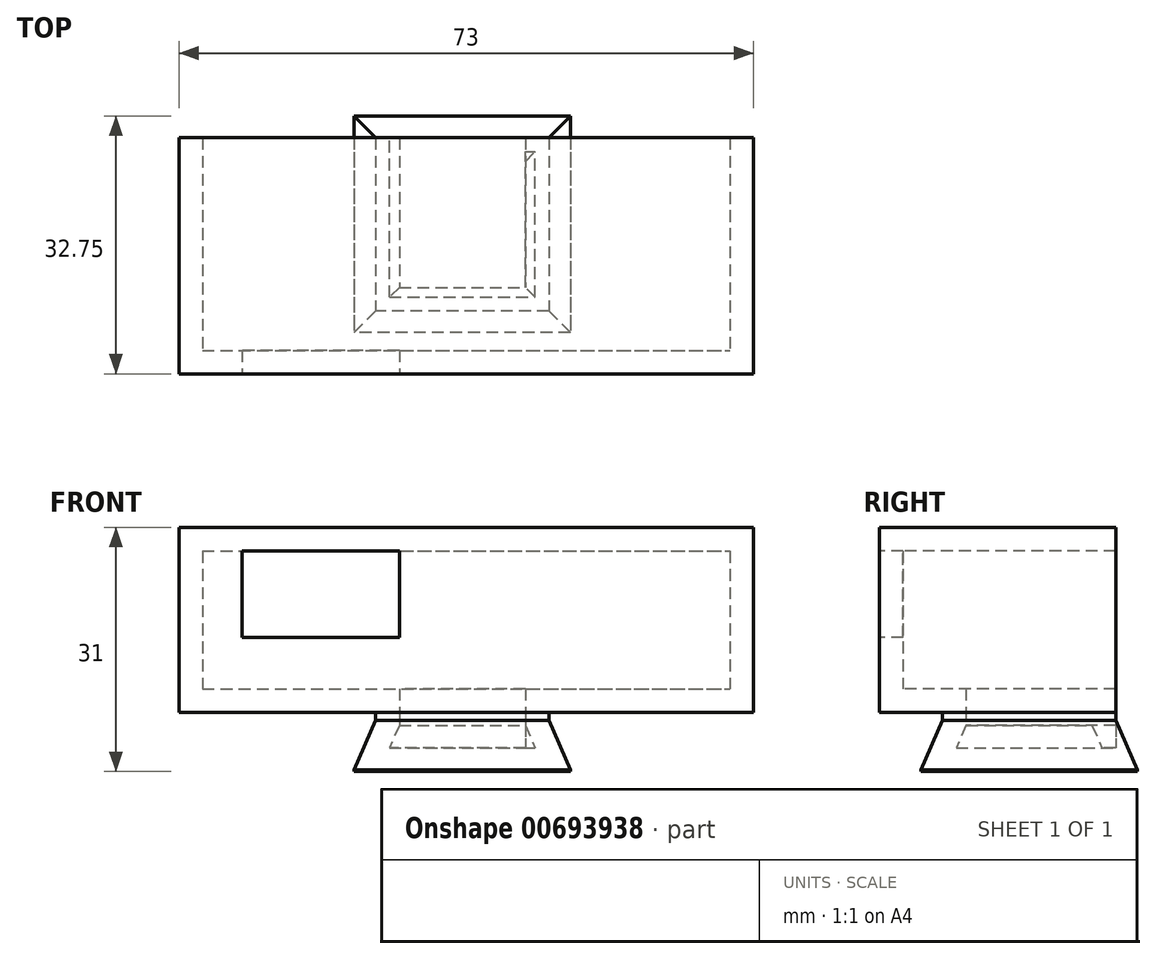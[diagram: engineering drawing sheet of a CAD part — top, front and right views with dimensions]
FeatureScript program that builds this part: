
annotation { "Feature Type Name" : "Feature", "Feature Type Description" : "" }
export const myFeature = defineFeature(function(context is Context, id is Id, definition is map)
    precondition{}
    {
        {
            var Q0;
            Q0=qCreatedBy(makeId("Top.planeOp"),FACE);
            var sketch = newSketch(context, id + "F0", { "sketchPlane" : qUnion([Q0])});
            skLineSegment(sketch, "E0.bottom", {"start": v(13.75, 13.75) * mm, "end": v(-13.75, 13.75) * mm});
            skLineSegment(sketch, "E0.top", {"start": v(13.75, -13.75) * mm, "end": v(-13.75, -13.75) * mm});
            skLineSegment(sketch, "E0.left", {"start": v(13.75, 13.75) * mm, "end": v(13.75, -13.75) * mm});
            skLineSegment(sketch, "E0.right", {"start": v(-13.75, 13.75) * mm, "end": v(-13.75, -13.75) * mm});
            skPoint(sketch, "E0.middle", {"position": v(0, 0) * mm});
            skLineSegment(sketch, "E1.bottom", {"start": v(11, 11) * mm, "end": v(-11, 11) * mm});
            skLineSegment(sketch, "E1.top", {"start": v(11, -11) * mm, "end": v(-11, -11) * mm});
            skLineSegment(sketch, "E1.left", {"start": v(11, 11) * mm, "end": v(11, -11) * mm});
            skLineSegment(sketch, "E1.right", {"start": v(-11, 11) * mm, "end": v(-11, -11) * mm});
            skLineSegment(sketch, "E2.bottom", {"start": v(-36, 11) * mm, "end": v(37, 11) * mm});
            skLineSegment(sketch, "E2.top", {"start": v(-36, -19) * mm, "end": v(37, -19) * mm});
            skLineSegment(sketch, "E2.left", {"start": v(-36, 11) * mm, "end": v(-36, -19) * mm});
            skLineSegment(sketch, "E2.right", {"start": v(37, 11) * mm, "end": v(37, -19) * mm});
            skSolve(sketch);
        }
        {
            var Q0;
            Q0=makeQuery(id+"F0.imprint","IMPRINT",FACE,{"disambiguationData":[TD([[makeQuery(id+"F0.imprint","IMPRINT",EDGE,{"derivedFrom":sQuery(id+"F0.wireOp",EDGE,"E1.bottom")}),1.0]])]});
            extrude(context, id + "F1", {"entities" : qUnion([Q0]), "depth" : 7.5 * mm, "offsetDistance" : 25 * mm, "hasSecondDirection" : true, "secondDirectionOppositeDirection" : false, "secondDirectionDepth" : 6.5 * mm});
        }
        {
            var Q0;
            {var subQ2=sQuery(id+"F0.wireOp",EDGE,"E0.bottom");Q0=makeQuery(id+"F0.imprint","IMPRINT",FACE,{"disambiguationData":[TD([[makeQuery(id+"F0.imprint","IMPRINT",EDGE,{"derivedFrom":subQ2}),1.0]])]});}
            var Q1;
            Q1=makeQuery(id+"F0.imprint","IMPRINT",FACE,{"disambiguationData":[TD([[makeQuery(id+"F0.imprint","IMPRINT",EDGE,{"derivedFrom":sQuery(id+"F0.wireOp",EDGE,"E1.bottom")}),1.0]])]});
            var Q2;
            {var subQ1=sQuery(id+"F0.wireOp",EDGE,"E0.top");Q2=makeQuery(id+"F0.imprint","IMPRINT",FACE,{"disambiguationData":[TD([[makeQuery(id+"F0.imprint","IMPRINT",EDGE,{"derivedFrom":subQ1}),-1.0]])]});}
            var Q3;
            Q3=makeQuery(id+"F0.imprint","IMPRINT",FACE,{"disambiguationData":[TD([[makeQuery(id+"F0.imprint","IMPRINT",EDGE,{"derivedFrom":sQuery(id+"F0.wireOp",EDGE,"E1.bottom")}),1.0]])]});
            extrude(context, id + "F2", {"entities" : qUnion([Q0, Q1, Q2, Q3]), "depth" : 0.2 * mm, "offsetDistance" : 25 * mm});
        }
        {
            var Q2;
            Q2=makeQuery(id+"F2.opExtrude","CAP_FACE",FACE,{"disambiguationData":[OSD([sQuery(id+"F0.wireOp",EDGE,"E0.bottom"),sQuery(id+"F0.wireOp",EDGE,"E0.top"),sQuery(id+"F0.wireOp",EDGE,"E0.left"),sQuery(id+"F0.wireOp",EDGE,"E0.right")])],"isStart":false});
            var Q3;
            Q3=makeQuery(id+"F1.opExtrude","CAP_FACE",FACE,{"disambiguationData":[OSD([sQuery(id+"F0.wireOp",EDGE,"E1.bottom"),sQuery(id+"F0.wireOp",EDGE,"E1.top"),sQuery(id+"F0.wireOp",EDGE,"E1.left"),sQuery(id+"F0.wireOp",EDGE,"E1.right")])],"isStart":true});
            loft(context, id + "F3", {"operationType" : NewBodyOperationType.ADD, "sheetProfilesArray" : [{ "sheetProfileEntities" : qUnion([Q2]) }, { "sheetProfileEntities" : qUnion([Q3]) }]});
        }
        {
            var Q0;
            {var subQ5=sQuery(id+"F0.wireOp",EDGE,"E0.top");Q0=makeQuery(id+"F0.imprint","IMPRINT",FACE,{"disambiguationData":[TD([[makeQuery(id+"F0.imprint","IMPRINT",EDGE,{"derivedFrom":subQ5}),1.0]])]});}
            var Q1;
            Q1=makeQuery(id+"F0.imprint","IMPRINT",FACE,{"disambiguationData":[TD([[makeQuery(id+"F0.imprint","IMPRINT",EDGE,{"derivedFrom":sQuery(id+"F0.wireOp",EDGE,"E1.bottom")}),1.0]])]});
            var Q2;
            {var subQ1=sQuery(id+"F0.wireOp",EDGE,"E0.top");Q2=makeQuery(id+"F0.imprint","IMPRINT",FACE,{"disambiguationData":[TD([[makeQuery(id+"F0.imprint","IMPRINT",EDGE,{"derivedFrom":subQ1}),-1.0]])]});}
            extrude(context, id + "F4", {"entities" : qUnion([Q0, Q1, Q2]), "operationType" : NewBodyOperationType.ADD, "depth" : 31 * mm, "offsetDistance" : 25 * mm, "hasSecondDirection" : true, "secondDirectionOppositeDirection" : false, "secondDirectionDepth" : 7.5 * mm});
        }
        {
            var Q0;
            {var subQ0=sQuery(id+"F0.wireOp",EDGE,"E1.bottom");Q0=makeQuery(id+"F4.boolean.opBoolean","MERGE",FACE,{"derivedFrom":[makeQuery(id+"F1.opExtrude","SWEPT_FACE",FACE,{"disambiguationData":[OSD([subQ0])]}),makeQuery(id+"F4.opExtrude","SWEPT_FACE",FACE,{"disambiguationData":[OSD([subQ0,sQuery(id+"F0.wireOp",EDGE,"E2.bottom")])]})]});}
            shell(context, id + "F5", {"entities" : qUnion([Q0]), "thickness" : 3 * mm});
        }
        {
            var Q0;
            Q0=makeQuery(id+"F4.opExtrude","SWEPT_FACE",FACE,{"disambiguationData":[OSD([sQuery(id+"F0.wireOp",EDGE,"E2.top")])]});
            var sketch = newSketch(context, id + "F6", { "sketchPlane" : qUnion([Q0])});
            skLineSegment(sketch, "E3.bottom", {"start": v(-28, 28) * mm, "end": v(-8, 28) * mm});
            skLineSegment(sketch, "E3.top", {"start": v(-28, 17) * mm, "end": v(-8, 17) * mm});
            skLineSegment(sketch, "E3.left", {"start": v(-28, 28) * mm, "end": v(-28, 17) * mm});
            skLineSegment(sketch, "E3.right", {"start": v(-8, 28) * mm, "end": v(-8, 17) * mm});
            skSolve(sketch);
        }
        {
            var Q0;
            Q0=makeQuery(id+"F6.imprint","IMPRINT",FACE,{"disambiguationData":[TD([[makeQuery(id+"F6.imprint","IMPRINT",EDGE,{"derivedFrom":sQuery(id+"F6.wireOp",EDGE,"E3.bottom")}),-1.0]])]});
            extrude(context, id + "F7", {"entities" : qUnion([Q0]), "operationType" : NewBodyOperationType.REMOVE, "endBound" : BoundingType.THROUGH_ALL, "oppositeDirection" : true, "depth" : 25 * mm, "offsetDistance" : 25 * mm});
        }
    });
